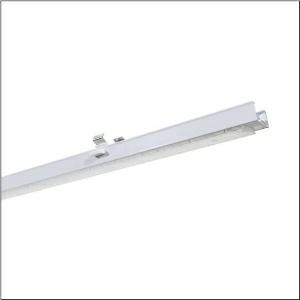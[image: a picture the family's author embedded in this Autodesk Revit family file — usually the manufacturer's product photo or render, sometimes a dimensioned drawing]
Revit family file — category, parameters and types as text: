
# Revit family: trunking_flex_31_51re12mb68b
name_source: partatom
category: Lighting Fixtures
units: mm (PartAtom-declared; Revit-internal decimal feet)

## family parameters
Cut with Voids When Loaded = No
Host = Face
Light Source = No
Part Type = Normal
Room Calculation Point = No
Round Connector Dimension = Use Diameter
Shared = No

## types (1)
- --- (1 x LED, 8000 lm, 50 W, 6500K)
    Apparent Load = 50 VA
    CIE Flux Codes = 65 91 98 99 100
    Color Rendering = 80
    Color Temperature = 6500K
    Default Elevation = 1800 mm
    Description = Trunking Flex 31, luminaire insert, of extruded aluminium section, coated, traffic white (RAL 9016), length: 1.472mm, width: 91mm, height: 53mm, LED rated luminous flux: 8.000lm, light colour: 865, control gear: ON/OFF Multilumen, with system connector: socket, mains connection: 220..240V, AC, 50/60Hz, rated input power: 50W, luminous flux adjustable on luminaire in four steps (4130/5610/6850/8000lm), connected load according to luminous flux setting (25/34/42/50W), primary light control with lens, of plastic, primary optical cover: cover, of PMMA, light emission: direct distribution, protection rating (complete): IP20, insulation class (complete): insulation class I (protective earthing), certification: CE, UKCA, impact resistance: IK02, permissible ambient temperature for indoor applications: -20..+40°C, packaging unit: 1 piece
    Height = 58 mm
    Lamp = 1 x LED
    Lamp Light Flux = 8000 lm
    Lamp Power = 50 W
    Lamp count = 1
    Length = 1472 mm
    Luminous efficacy = 160 lm/W
    Manufacturer = Siteco
    ModVariant = No
    Model = 51RE12MB68B
    Mounting Place = Ceiling
    Mounting Type = Pendant
    Number of Poles = 1
    OnlyDefault = Yes
    Power Factor = 1
    Product Name = Trunking Flex 31
    Product group = luminaire insert
    ProductGroupID = 902
    Protection Class = Protection class I
    Protection Degree = IP 20
    RLX_Detail_Level = 1
    RLX_Emergency_Light_Flux = 0 lm
    RLX_Emergency_Type = 0
    RLX_Emergency_Type_DB = No
    RlxData = <blob elided: 20357 chars, md5=9a32f93c>
    Socket = socket
    Standby Power = 0 W
    System Light Flux = 8000 lm
    System Power = 50 W
    Type Comments = factory setting: luminous flux: 100 % | (ON | ON) | 300 mA
    Type Image = l_1266702.jpg
    URL = http://relux.com
    VarID = @adj_059118
    Voltage = 0 V
    Weight = 0.00 kg
    Width = 65 mm

## geometry (parser evidence)
native form markers: Blend x4, Sweep x11
no freeform markers — native parametric forms only
